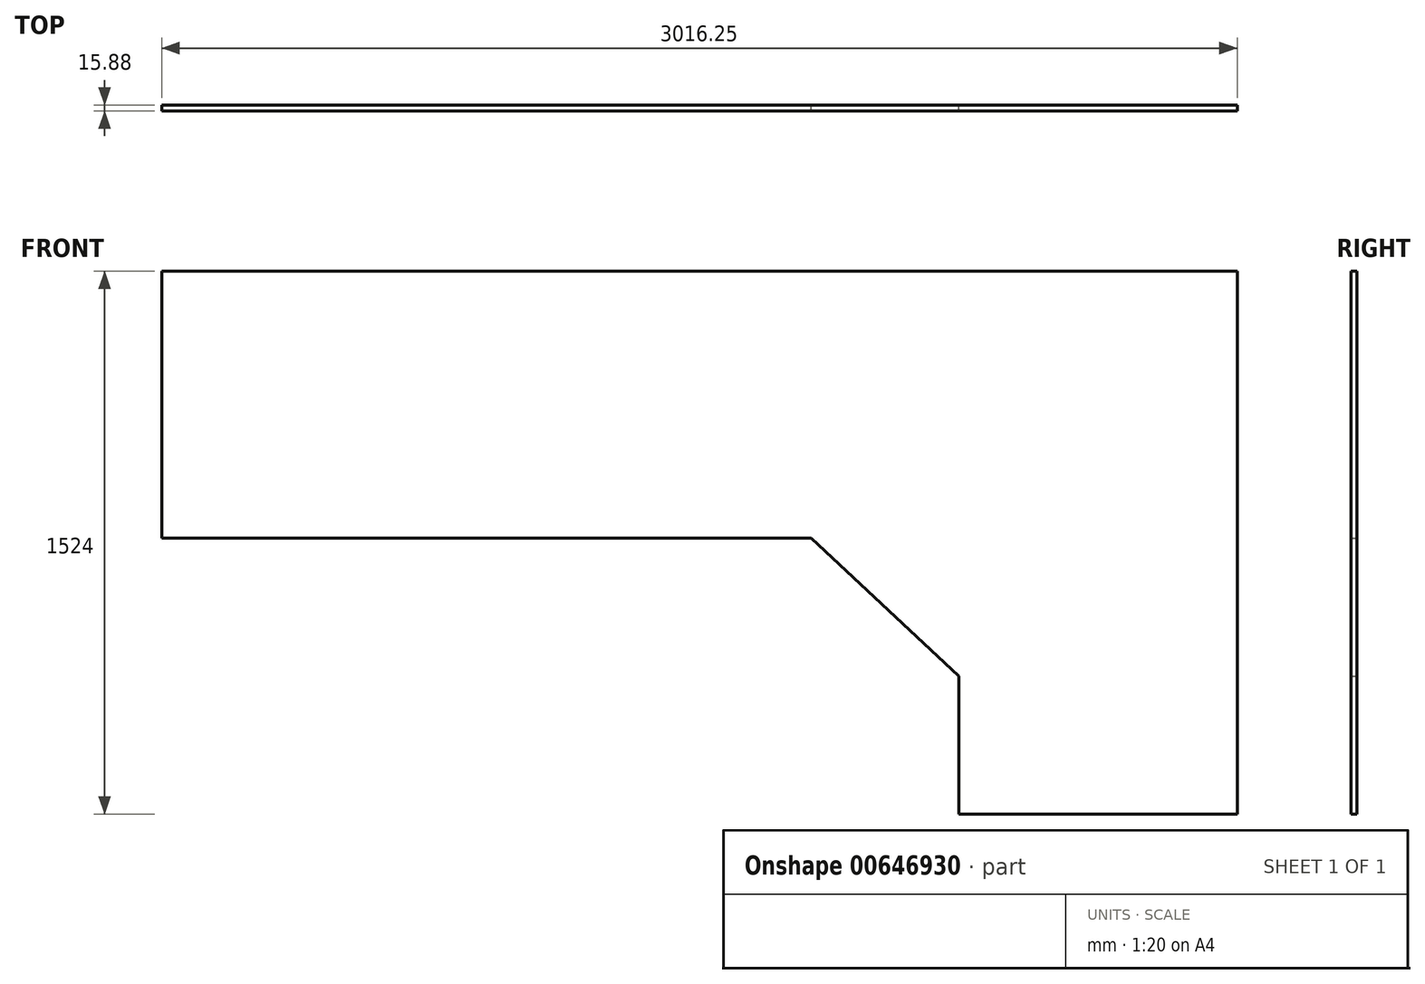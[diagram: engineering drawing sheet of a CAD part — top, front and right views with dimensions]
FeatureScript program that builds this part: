
annotation { "Feature Type Name" : "Feature", "Feature Type Description" : "" }
export const myFeature = defineFeature(function(context is Context, id is Id, definition is map)
    precondition{}
    {
        {
            var Q0;
            Q0=qCreatedBy(makeId("Front.planeOp"),FACE);
            var sketch = newSketch(context, id + "F0", { "sketchPlane" : qUnion([Q0])});
            skLineSegment(sketch, "E0", {"start": v(-65.7, -79.1) * mm, "end": v(2950.55, -79.1) * mm});
            skLineSegment(sketch, "E1", {"start": v(2950.55, -79.1) * mm, "end": v(2950.55, -1603.1) * mm});
            skLineSegment(sketch, "E2", {"start": v(2950.55, -1603.1) * mm, "end": v(2169.5, -1603.1) * mm});
            skLineSegment(sketch, "E3", {"start": v(2169.5, -1603.1) * mm, "end": v(2169.5, -1215.75) * mm});
            skLineSegment(sketch, "E4", {"start": v(-65.7, -79.1) * mm, "end": v(-65.7, -828.4) * mm});
            skLineSegment(sketch, "E5", {"start": v(-65.7, -828.4) * mm, "end": v(1756.4, -828.4) * mm});
            skLineSegment(sketch, "E6", {"start": v(1756.4, -828.4) * mm, "end": v(2169.5, -1215.75) * mm});
            skSolve(sketch);
        }
        {
            var Q0;
            Q0 = qSketchRegion(id + "F0", true);
            extrude(context, id + "F1", {"entities" : qUnion([Q0]), "depth" : 15.88 * mm, "offsetDistance" : 25.4 * mm});
        }
    });
